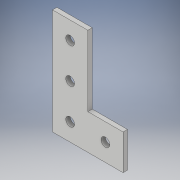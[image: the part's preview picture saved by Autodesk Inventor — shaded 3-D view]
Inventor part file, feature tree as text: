
AUTODESK INVENTOR PART (.ipt)
format: ipt  version: 2018 (Build 220112000, 112)  size: 114,176 bytes
history: native  units: in
note: dims shown in document units (in); Inventor stores cm internally (conversion verified against a paired STEP export)
features: hole x4, extrude x1, sketch x1
ambient origin geometry x8: Origin, YZ Plane, XZ Plane, XY Plane, X Axis, Y Axis, Z Axis, Center Point
bodies: Solid1 (feature_tree), Body1 (feature_tree)
feature tree (6):
  extrude  "Extrusion1"  Depth=1.0in
  hole  "Hole1"  [1 undecoded]
  hole  "Hole2"  [1 undecoded]
  hole  "Hole3"  [1 undecoded]
  hole  "Hole4"  [1 undecoded]
  sketch  "Sketch1"  dims[d0=1.0in d1=1.0in d2=1.0in d3=0.0in d4=1.0in d5=1.0in d6=0.25in d7=0.75in d8=0.375in d9=0.25in d10=0.5635in d11=1.0in d12=0.8108in d13=1.0in d14=1.0in d15=0.25in d16=0.75in d17=0.375in d18=0.25in d19=0.5635in d20=1.0in d21=0.8108in d22=1.0in d23=1.0in d24=0.25in d25=0.75in d26=0.375in d27=0.25in d28=0.5635in d29=1.0in d30=0.8108in d31=1.0in d32=1.0in d33=0.25in d34=0.75in d35=0.375in d36=0.25in d37=0.5635in d38=1.0in d39=0.8108in]
note: 4 required parameter values undecoded (feature->parameter linkage not recoverable at this tier; creation-order binding heuristic only, values carry confidence <= 0.55)
